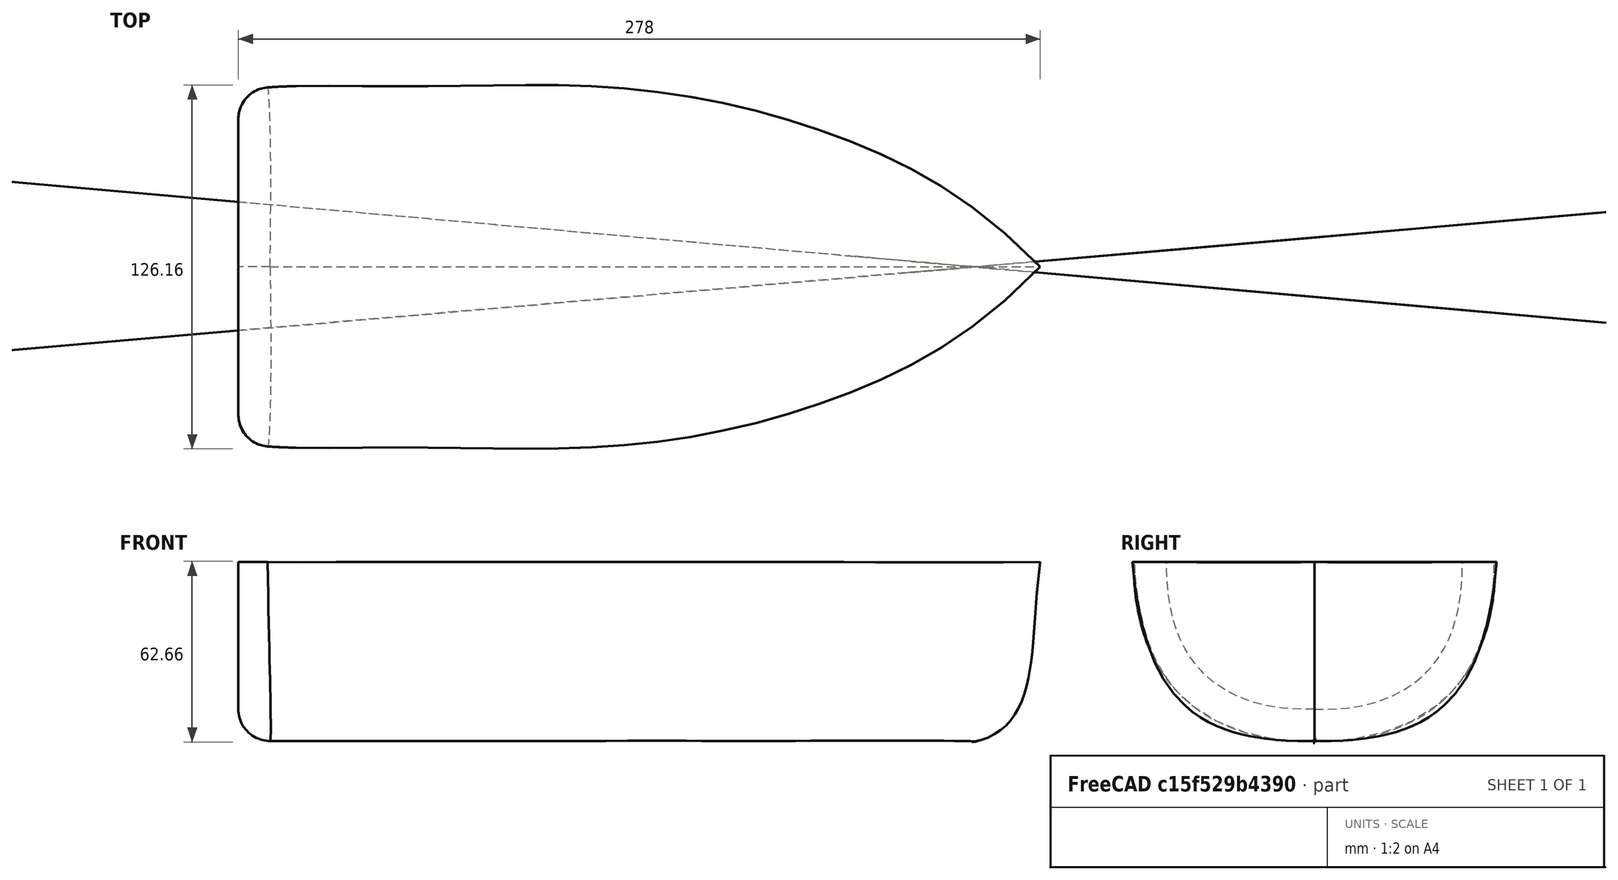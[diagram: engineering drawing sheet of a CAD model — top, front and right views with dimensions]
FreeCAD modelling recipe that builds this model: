
FCSTD DOCUMENT  (FreeCAD 0.16RUnknown)
Label: footyv2
License: All rights reserved
LicenseURL: http://en.wikipedia.org/wiki/All_rights_reserved
objects: Part::Part2DObjectPython×7, Part::Feature×3, Part::Mirroring×2, Part::RuledSurface×2, Mesh::Feature×1, Part::Loft×1, PartDesign::Fillet×1, Sketcher::SketchObject×1, PartDesign::Pad×1, Part::Cut×1
note: 20 computed .brp shape members not serialized (recipe doc carries the construction recipe); baked Part::Feature solids carry a one-line shape summary decoded from their .brp

FEATURE [Mesh::Feature] pelicase
  Placement = pos=(92.1026,0.33513,12.2478) rot=(0.000287,-0.002204,0.999998;3.14459rad)
FEATURE [Part::Part2DObjectPython] BezCurve  # Draft 2D object (typed FeaturePython)
  Closed = false
  Degree = 3
  MakeFace = true
  Points = (4) [(0,0,0),(0,34,-2),(0,62,16),(0,61,62)]
FEATURE [Part::Part2DObjectPython] BezCurve001  # Draft 2D object (typed FeaturePython)
  Closed = false
  Degree = 3
  MakeFace = true
  Placement = pos=(20,0,0) rot=(0,0,1;0rad)
  Points = (4) [(0,0,0),(0,34,-1),(0,62.6975,16.9663),(0,62.6975,61.9663)]
FEATURE [Part::Part2DObjectPython] BezCurve002  # Draft 2D object (typed FeaturePython)
  Closed = false
  Degree = 3
  MakeFace = true
  Placement = pos=(150,0,0) rot=(0,0,1;0rad)
  Points = (4) [(0,0,0),(0,40,0),(0,58,16),(0,60,62)]
FEATURE [Part::Part2DObjectPython] BezCurve005  # Draft 2D object (typed FeaturePython)
  Closed = false
  Degree = 3
  MakeFace = true
  Placement = pos=(200,0,0) rot=(0,0,1;0rad)
  Points = (4) [(0,0,0),(0,36,3),(0,48,21),(0,48,62)]
FEATURE [Part::Part2DObjectPython] BezCurve006  # Draft 2D object (typed FeaturePython)
  Closed = false
  Degree = 3
  MakeFace = true
  Placement = pos=(-11,0,0) rot=(0,0,1;0rad)
  Points = (4) [(265.382,0,-0.397799),(290,0,4),(285,0,34),(289,0,62)]
FEATURE [Part::Part2DObjectPython] BezCurve004  # Draft 2D object (typed FeaturePython)
  Closed = false
  Degree = 3
  MakeFace = true
  Placement = pos=(246,0,0) rot=(0,0,1;0rad)
  Points = (4) [(0,0,0),(0,15.3921,7.52249),(0,24.4707,18.9061),(0,26.4707,61.9061)]
FEATURE [Part::Part2DObjectPython] BezCurve007  # Draft 2D object (typed FeaturePython)
  Closed = false
  Degree = 3
  MakeFace = true
  Placement = pos=(90,0,0) rot=(0,0,1;0rad)
  Points = (4) [(0,0,0),(0,39,-1),(0,59,13),(0,63,62)]
FEATURE [Part::Loft] Loft
  Closed = false
  Ruled = false
  Sections = -> [BezCurve,BezCurve001,BezCurve007,BezCurve002,BezCurve005,BezCurve004,BezCurve006]
  Solid = false
FEATURE [Part::Mirroring] Part__Mirroring  label="Loft (Mirror #1)"
  Base = (0,0,0)
  Normal = (0,1,0)
  Source = -> Loft
FEATURE [Part::Mirroring] Part__Mirroring001  label="BezCurve (Mirror #2)"
  Base = (0,0,0)
  Normal = (0,1,0)
  Source = -> BezCurve
FEATURE [Part::RuledSurface] Ruled_Surface
  Curve1 = -> BezCurve
  Curve2 = -> Part__Mirroring001
  Orientation = 0
FEATURE [Part::RuledSurface] Ruled_Surface001
  Curve1 = -> Part__Mirroring [Edge2]
  Curve2 = -> Loft [Edge2]
  Orientation = 0
FEATURE [Part::Feature] Shell
  shape: bbox 279 x 192.9 x 126.8 mm, 4 faces, 0 solids (baked)
FEATURE [Part::Feature] Solid
  Placement = pos=(-100,0,0) rot=(0,0,1;0rad)
  shape: bbox 279 x 192.9 x 126.8 mm, 4 faces (baked)
FEATURE [PartDesign::Fillet] Fillet
  Base = -> Solid [Edge5,Edge1]
  Placement = pos=(-100,0,0) rot=(0,0,1;0rad)
  Radius = 11
FEATURE [Part::Feature] Fillet001
  shape: bbox 279 x 192.9 x 126.8 mm, 6 faces (baked)
FEATURE [Sketcher::SketchObject] Sketch
  Placement = pos=(0,0,35) rot=(0,0,1;0rad)
  sketch-geometry (4):
    g0: LineSegment StartX=-122.915 StartY=101.405 StartZ=0 EndX=240.709 EndY=101.405 EndZ=0
    g1: LineSegment StartX=240.709 StartY=101.405 StartZ=0 EndX=240.709 EndY=-98.3321 EndZ=0
    g2: LineSegment StartX=240.709 StartY=-98.3321 StartZ=0 EndX=-122.915 EndY=-98.3321 EndZ=0
    g3: LineSegment StartX=-122.915 StartY=-98.3321 StartZ=0 EndX=-122.915 EndY=101.405 EndZ=0
  constraints (8):
    c: Coincident(g0,g1)
    c: Coincident(g1,g2)
    c: Coincident(g2,g3)
    c: Coincident(g3,g0)
    c: Horizontal(g0)
    c: Horizontal(g2)
    c: Vertical(g1)
    c: Vertical(g3)
FEATURE [PartDesign::Pad] Pad
  Length = 150
  Length2 = 100
  Placement = pos=(0,0,35) rot=(0,0,1;0rad)
  Sketch = -> Sketch
  Type = 0
FEATURE [Part::Cut] Cut
  Base = -> Fillet001
  Tool = -> Pad
